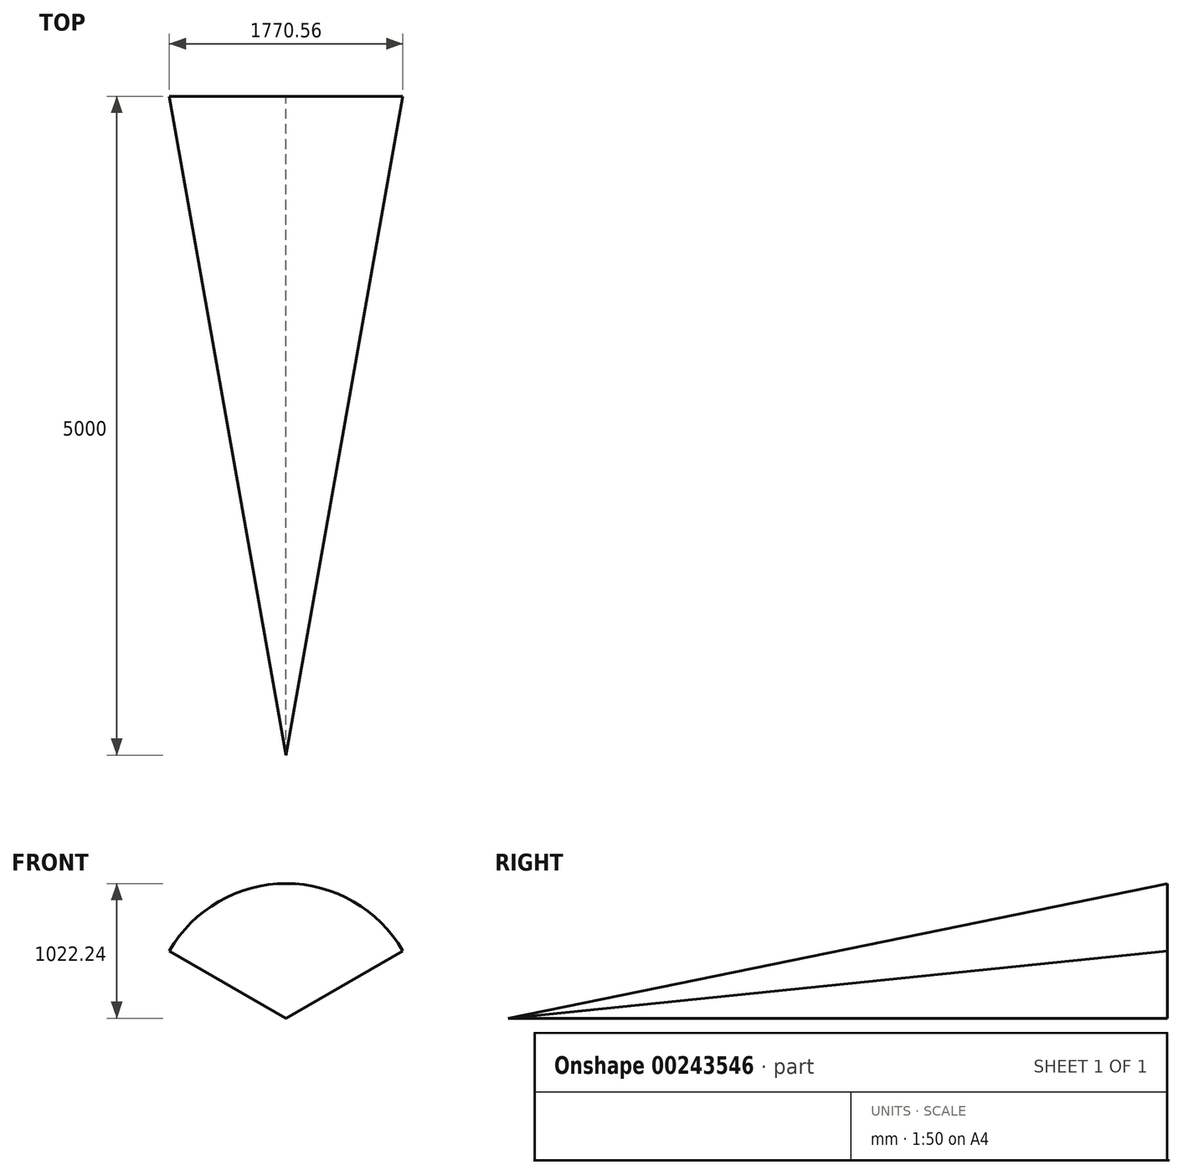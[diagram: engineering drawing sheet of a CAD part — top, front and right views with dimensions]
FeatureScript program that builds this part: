
annotation { "Feature Type Name" : "Feature", "Feature Type Description" : "" }
export const myFeature = defineFeature(function(context is Context, id is Id, definition is map)
    precondition{}
    {
        {
            var Q0;
            Q0=qCreatedBy(makeId("Right.planeOp"),FACE);
            var sketch = newSketch(context, id + "F0", { "sketchPlane" : qUnion([Q0])});
            skLineSegment(sketch, "E0.left", {"start": v(-3500, 520.89) * mm, "end": v(-3500, -1000) * mm});
            skPoint(sketch, "E0.middle", {"position": v(0, 0) * mm});
            skLineSegment(sketch, "E1", {"start": v(-3500, -1000) * mm, "end": v(-3500, 520.89) * mm});
            skLineSegment(sketch, "E2", {"start": v(-3500, -1000) * mm, "end": v(-8500, -1000) * mm});
            skLineSegment(sketch, "E3", {"start": v(-8500, -1000) * mm, "end": v(-8500, -501.35) * mm});
            skLineSegment(sketch, "E4", {"start": v(-8500, -501.35) * mm, "end": v(-3500, -1000) * mm});
            skLineSegment(sketch, "E5", {"start": v(-8500, -501.35) * mm, "end": v(-3500, -501.35) * mm});
            skLineSegment(sketch, "E6", {"start": v(-8500, -501.35) * mm, "end": v(-3500, 520.89) * mm});
            skSolve(sketch);
        }
        {
            var Q0;
            {var subQ2=sQuery(id+"F0.wireOp",EDGE,"E5");Q0=makeQuery(id+"F0.imprint","IMPRINT",FACE,{"disambiguationData":[TD([[makeQuery(id+"F0.imprint","IMPRINT",EDGE,{"derivedFrom":subQ2}),1.0]])]});}
            var Q1;
            Q1=sQuery(id+"F0.wireOp",EDGE,"E5");
            revolve(context, id + "F1", {"entities" : qUnion([Q0]), "axis" : qUnion([Q1]), "revolveType" : RevolveType.SYMMETRIC, "angle" : 120 * degree});
        }
    });
